# Revit family: Shower_Set-GROHE-Tempesta_Cosmopolitan-27577002
name_source: partatom
category: Plumbing Fixtures
units: mm (PartAtom-declared; Revit-internal decimal feet)

## family parameters
Cut with Voids When Loaded = No
Host = Face
OmniClass Number = 23.45.05.14.17
OmniClass Title = Showers
Part Type = Normal
Room Calculation Point = No
Round Connector Dimension = Use Diameter
Shared = Yes

## types (1)
- 27577002
    69” RelexaFlex Plastic shower hose (28 154) = Yes
    ASME A112.18.1/CSA B125.1 = Yes
    Assembly Code = D2010710
    CW Connection = Yes
    CWFU = 3
    Cold Water Connection Diameter = 1/2"
    Cold Water Connection Radius = 1/4"
    Default Elevation = 74"
    Description = Tempesta Cosmopolitan 24" Shower Slide Bar Kit-4 Sprays
    Energy Policy Act of 1992 = Yes
    Finish = Metal-Grohe-002-StarLight Chrome
    Flow Rate = 2.5 gpm (9.5 L/min)
    HW Connection = Yes
    HWFU = 3
    Hand Shower Geometry = 27575 Shower Handle : 27575 Hand Shower 002
    Height = 24 7/16"
    Hot Water Connection Diameter = 1"
    Hot Water Connection Radius = 1/4"
    Installation Type = Wall Mounted
    Length = 2 3/4"
    Manufacturer = Grohe
    Massachusetts Plumbing Board Approved = Yes
    Material = Metal-Grohe-002-StarLight Chrome
    Model = 27577002
    Product Documentation Link = https://lixil.cdn.celum.cloud
    Product Page URL = https://www.grohe.us
    Revised Date = 08/01/2023
    Tempered Connection Diameter = 1/2"
    Tempered Connection Radius = 1/4"
    URL = https://www.grohe.us
    Vent Connection = No
    WFU = 4
    Waste Connection = No
    Width = 2 7/8"
    cUPC Compliant = Yes

## geometry (parser evidence)
native form markers: Sweep x8
no freeform markers — native parametric forms only
